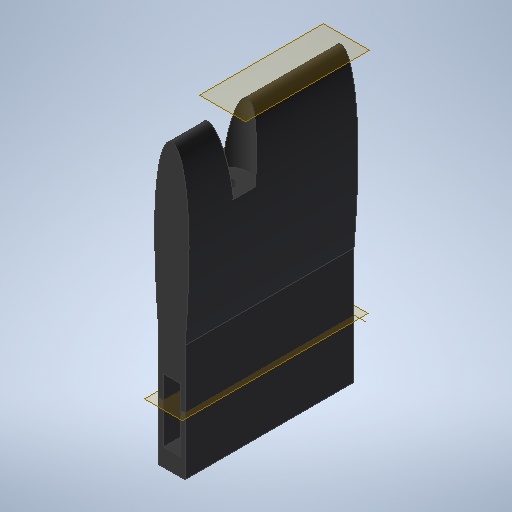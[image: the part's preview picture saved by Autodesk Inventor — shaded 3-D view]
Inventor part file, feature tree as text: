
AUTODESK INVENTOR PART (.ipt)
format: ipt  version: 2025.2 (Build 292293000, 293)  size: 351,744 bytes
history: native  units: in
note: dims shown in document units (in); Inventor stores cm internally (conversion verified against a paired STEP export)
features: extrude x7, other x7, sketch x7, plane x5, projected_geometry x2, mirror x1
ambient origin geometry x8: Origin, YZ Plane, XZ Plane, XY Plane, X Axis, Y Axis, Z Axis, Center Point
bodies: Solid1 (feature_tree)
feature tree (29):
  plane  "Work Plane1"
  extrude  "Extrusion1"  Depth=4.7244in TaperAngle=0.0deg
  plane  "Work Plane3"
  other  "Work Axis1"
  plane  "Work Plane4"
  other  "Work Point1"
  extrude  "Extrusion2"  Depth=1.8899in TaperAngle=0.0deg
  other  "Work Axis2"
  plane  "Work Plane5"
  extrude  "Extrusion7"  Depth=0.5in
  extrude  "Extrusion8"  Depth=0.4724in TaperAngle=0.0deg
  extrude  "Extrusion9"  Depth=4.7865in TaperAngle=0.0deg
  extrude  "Extrusion10"  Depth=1.7717in
  extrude  "Extrusion11"  Depth=0.906in
  plane  "Work Plane6"
  mirror  "Mirror1"
  sketch  "Sketch1"  dims[d2=8.0in d3=4.7244in d4=0.0in]
  sketch  "Sketch3"  dims[d8=1.125in d11=1.8899in d12=0.0in]
  sketch  "Sketch9"  dims[d15=13.0in d16=0.5in]
  sketch  "Sketch10"  dims[d33=0.4724in d37=3.6411in d38=0.0in]
  projected_geometry  "Projected Loop2"
  sketch  "Sketch11"  dims[d39=0.4in d40=4.7865in d41=0.0in]
  projected_geometry  "Projected Loop3"
  sketch  "Sketch12"  dims[d42=1.7717in d44=2.2658in]
  sketch  "Sketch13"  dims[d45=0.4724in d46=0.906in d47=2.081in d48=1.084in d49=0.0in d50=1.22in d51=0.2559in d52=0.0in d53=0.0984in d54=0.0984in d55=0.0787in d56=0.0787in d57=0.0787in d58=0.0787in d59=0.8661in d60=0.0in d61=90.0deg d13=0.5in d14=0.0344in]
  other  "Work Axis3"
  other  "<userpath>\OneDrive\Documents\Spring 2025\Senior Design\Tail\TailAssembly.iam"
  other  "TailAssembly.iam"
  other  "MiddleTailLeft:1"
